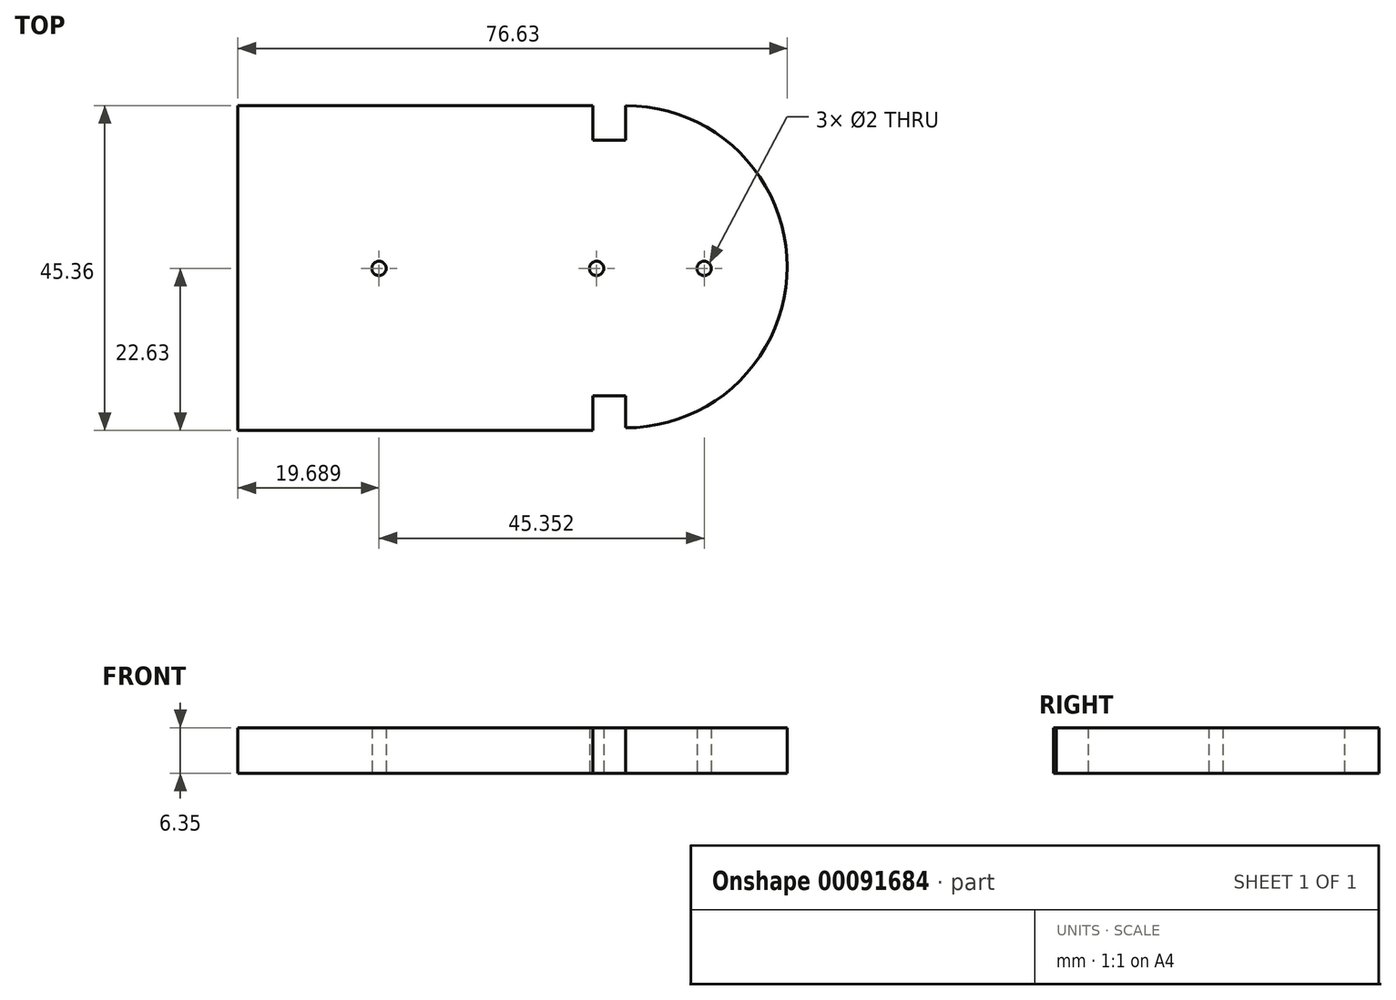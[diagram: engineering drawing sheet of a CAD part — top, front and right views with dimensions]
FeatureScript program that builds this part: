
annotation { "Feature Type Name" : "Feature", "Feature Type Description" : "" }
export const myFeature = defineFeature(function(context is Context, id is Id, definition is map)
    precondition{}
    {
        {
            var Q0;
            Q0=qCreatedBy(makeId("Top.planeOp"),FACE);
            var sketch = newSketch(context, id + "F0", { "sketchPlane" : qUnion([Q0])});
            skPoint(sketch, "E0.middle", {"position": v(0, 0) * mm});
            skPoint(sketch, "E1.first.point", {"position": v(-2, 0) * mm});
            skPoint(sketch, "E1.second.point", {"position": v(17.57, 0) * mm});
            skPoint(sketch, "E1.third.point", {"position": v(14.87, -6.61) * mm});
            skPoint(sketch, "E2.second.point", {"position": v(27.34, 0) * mm});
            skPoint(sketch, "E2.third.point", {"position": v(25.92, 4.68) * mm});
            skLineSegment(sketch, "E3.bottom", {"start": v(-44.45, -22.63) * mm, "end": v(5.08, -22.63) * mm});
            skLineSegment(sketch, "E3.top", {"start": v(-44.45, 22.73) * mm, "end": v(5.08, 22.73) * mm});
            skLineSegment(sketch, "E3.left", {"start": v(-44.45, -22.63) * mm, "end": v(-44.45, 22.73) * mm});
            skPoint(sketch, "E4", {"position": v(5.08, 22.73) * mm});
            skPoint(sketch, "E5", {"position": v(9.65, 22.73) * mm});
            skPoint(sketch, "E6", {"position": v(5.08, -22.63) * mm});
            skPoint(sketch, "E7", {"position": v(9.65, -22.25) * mm});
            skLineSegment(sketch, "E8", {"start": v(5.08, 22.73) * mm, "end": v(5.08, 17.9) * mm});
            skLineSegment(sketch, "E9", {"start": v(5.08, 17.9) * mm, "end": v(9.65, 17.9) * mm});
            skLineSegment(sketch, "E10", {"start": v(9.65, 17.9) * mm, "end": v(9.65, 22.73) * mm});
            skLineSegment(sketch, "E11", {"start": v(5.08, -22.63) * mm, "end": v(5.08, -17.8) * mm});
            skLineSegment(sketch, "E12", {"start": v(5.08, -17.8) * mm, "end": v(9.65, -17.8) * mm});
            skLineSegment(sketch, "E13", {"start": v(9.65, -17.8) * mm, "end": v(9.65, -22.25) * mm});
            skLineSegment(sketch, "E14.bottom", {"start": v(-80.42, 201.87) * mm, "end": v(135.48, 201.87) * mm});
            skLineSegment(sketch, "E14.top", {"start": v(-80.42, -77.53) * mm, "end": v(135.48, -77.53) * mm});
            skLineSegment(sketch, "E14.left", {"start": v(-80.42, 201.87) * mm, "end": v(-80.42, -77.53) * mm});
            skLineSegment(sketch, "E14.right", {"start": v(135.48, 201.87) * mm, "end": v(135.48, -77.53) * mm});
            skArc(sketch, "E15", {"start": v(9.65, -22.25) * mm, "mid": v(32.18, 0.24) * mm, "end": v(9.65, 22.73) * mm});
            skCircle(sketch, "E16", {"center": v(-24.76, 0) * mm, "radius": 1 * mm});
            skCircle(sketch, "E17", {"center": v(5.59, 0) * mm, "radius": 1 * mm});
            skCircle(sketch, "E18", {"center": v(20.6, 0) * mm, "radius": 1 * mm});
            skSolve(sketch);
        }
        {
            var Q0;
            Q0=makeQuery(id+"F0.imprint","IMPRINT",FACE,{"disambiguationData":[TD([[makeQuery(id+"F0.imprint","IMPRINT",EDGE,{"derivedFrom":sQuery(id+"F0.wireOp",EDGE,"E3.bottom")}),1.0]])]});
            extrude(context, id + "F1", {"entities" : qUnion([Q0]), "depth" : 6.35 * mm});
        }
    });
